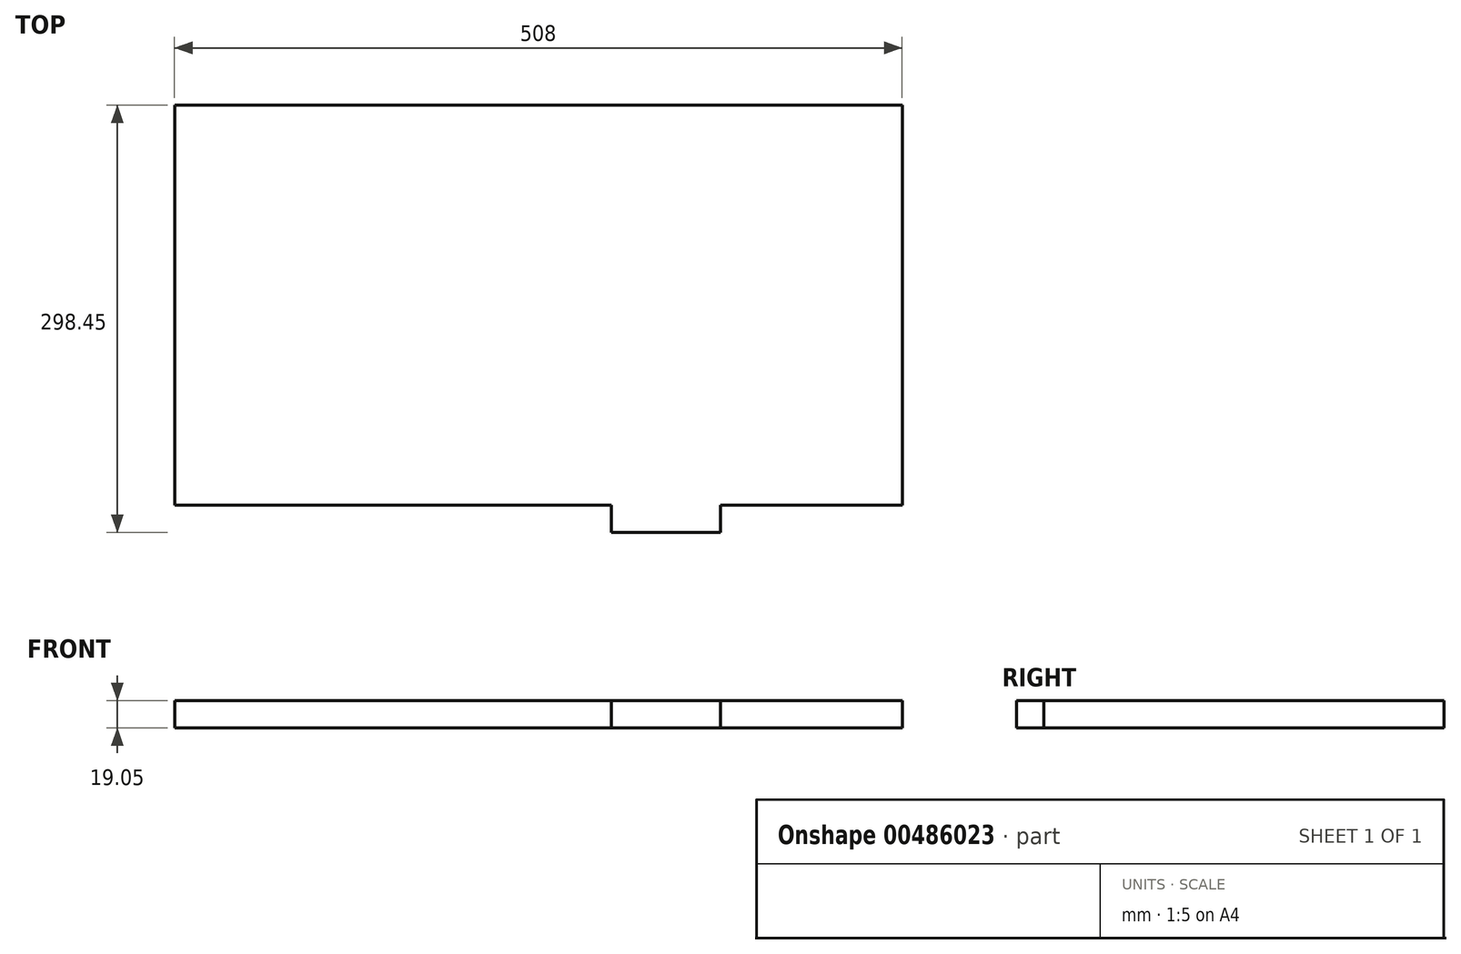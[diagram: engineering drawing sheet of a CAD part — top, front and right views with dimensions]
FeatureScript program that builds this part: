
annotation { "Feature Type Name" : "Feature", "Feature Type Description" : "" }
export const myFeature = defineFeature(function(context is Context, id is Id, definition is map)
    precondition{}
    {
        {
            var Q0;
            Q0=qCreatedBy(makeId("Top.planeOp"),FACE);
            var sketch = newSketch(context, id + "F0", { "sketchPlane" : qUnion([Q0])});
            skLineSegment(sketch, "E0.bottom", {"start": v(-239.09, 267.64) * mm, "end": v(268.91, 267.64) * mm});
            skLineSegment(sketch, "E0.top", {"start": v(-239.09, -11.76) * mm, "end": v(268.91, -11.76) * mm});
            skLineSegment(sketch, "E0.left", {"start": v(-239.09, 267.64) * mm, "end": v(-239.09, -11.76) * mm});
            skLineSegment(sketch, "E0.right", {"start": v(268.91, 267.64) * mm, "end": v(268.91, -11.76) * mm});
            skSolve(sketch);
        }
        {
            var Q0;
            Q0 = qSketchRegion(id + "F0", true);
            extrude(context, id + "F1", {"entities" : qUnion([Q0]), "depth" : 19.05 * mm, "offsetDistance" : 25.4 * mm});
        }
        {
            var Q0;
            Q0=makeQuery(id+"F1.opExtrude","SWEPT_FACE",FACE,{"disambiguationData":[OSD([sQuery(id+"F0.wireOp",EDGE,"E0.top")])]});
            var sketch = newSketch(context, id + "F2", { "sketchPlane" : qUnion([Q0])});
            skLineSegment(sketch, "E1.bottom", {"start": v(-239.09, 19.05) * mm, "end": v(-112.09, 19.05) * mm});
            skLineSegment(sketch, "E1.top", {"start": v(-239.09, 19.05) * mm, "end": v(-112.09, 19.05) * mm});
            skLineSegment(sketch, "E1.left", {"start": v(-239.09, 19.05) * mm, "end": v(-239.09, 19.05) * mm});
            skLineSegment(sketch, "E1.right", {"start": v(-112.09, 19.05) * mm, "end": v(-112.09, 19.05) * mm});
            skLineSegment(sketch, "E2.bottom", {"start": v(-112.09, 0) * mm, "end": v(-35.89, 0) * mm});
            skLineSegment(sketch, "E2.top", {"start": v(-112.09, 0) * mm, "end": v(-35.89, 0) * mm});
            skLineSegment(sketch, "E2.left", {"start": v(-112.09, 0) * mm, "end": v(-112.09, 0) * mm});
            skLineSegment(sketch, "E2.right", {"start": v(-35.89, 0) * mm, "end": v(-35.89, 0) * mm});
            skLineSegment(sketch, "E3.bottom", {"start": v(-35.89, 19.05) * mm, "end": v(-112.09, 19.05) * mm});
            skLineSegment(sketch, "E3.top", {"start": v(-35.89, 19.05) * mm, "end": v(-112.09, 19.05) * mm});
            skLineSegment(sketch, "E3.left", {"start": v(-35.89, 19.05) * mm, "end": v(-35.89, 19.05) * mm});
            skLineSegment(sketch, "E4", {"start": v(-112.09, 19.05) * mm, "end": v(-112.09, 0) * mm});
            skLineSegment(sketch, "E5", {"start": v(-35.89, 19.05) * mm, "end": v(-35.89, 0) * mm});
            skLineSegment(sketch, "E6", {"start": v(268.91, 19.05) * mm, "end": v(141.91, 19.05) * mm});
            skLineSegment(sketch, "E7", {"start": v(141.91, 19.05) * mm, "end": v(141.91, 0) * mm});
            skLineSegment(sketch, "E8", {"start": v(141.91, 0) * mm, "end": v(65.71, 0) * mm});
            skLineSegment(sketch, "E9", {"start": v(65.71, 0) * mm, "end": v(65.71, 19.05) * mm});
            skLineSegment(sketch, "E10", {"start": v(65.71, 19.05) * mm, "end": v(141.91, 19.05) * mm});
            skSolve(sketch);
        }
        {
            var Q0;
            Q0=makeQuery(id+"F2.imprint","IMPRINT",FACE,{"disambiguationData":[TD([[makeQuery(id+"F2.imprint","IMPRINT",EDGE,{"derivedFrom":sQuery(id+"F2.wireOp",EDGE,"E7")}),-1.0]])]});
            var Q1;
            Q1=makeQuery(id+"F2.imprint","IMPRINT",FACE,{"disambiguationData":[TD([[makeQuery(id+"F2.imprint","IMPRINT",EDGE,{"derivedFrom":sQuery(id+"F2.wireOp",EDGE,"E2.top")}),1.0]])]});
            extrude(context, id + "F3", {"entities" : qUnion([Q0, Q1]), "operationType" : NewBodyOperationType.ADD, "depth" : 19.05 * mm, "offsetDistance" : 25.4 * mm});
        }
    });
